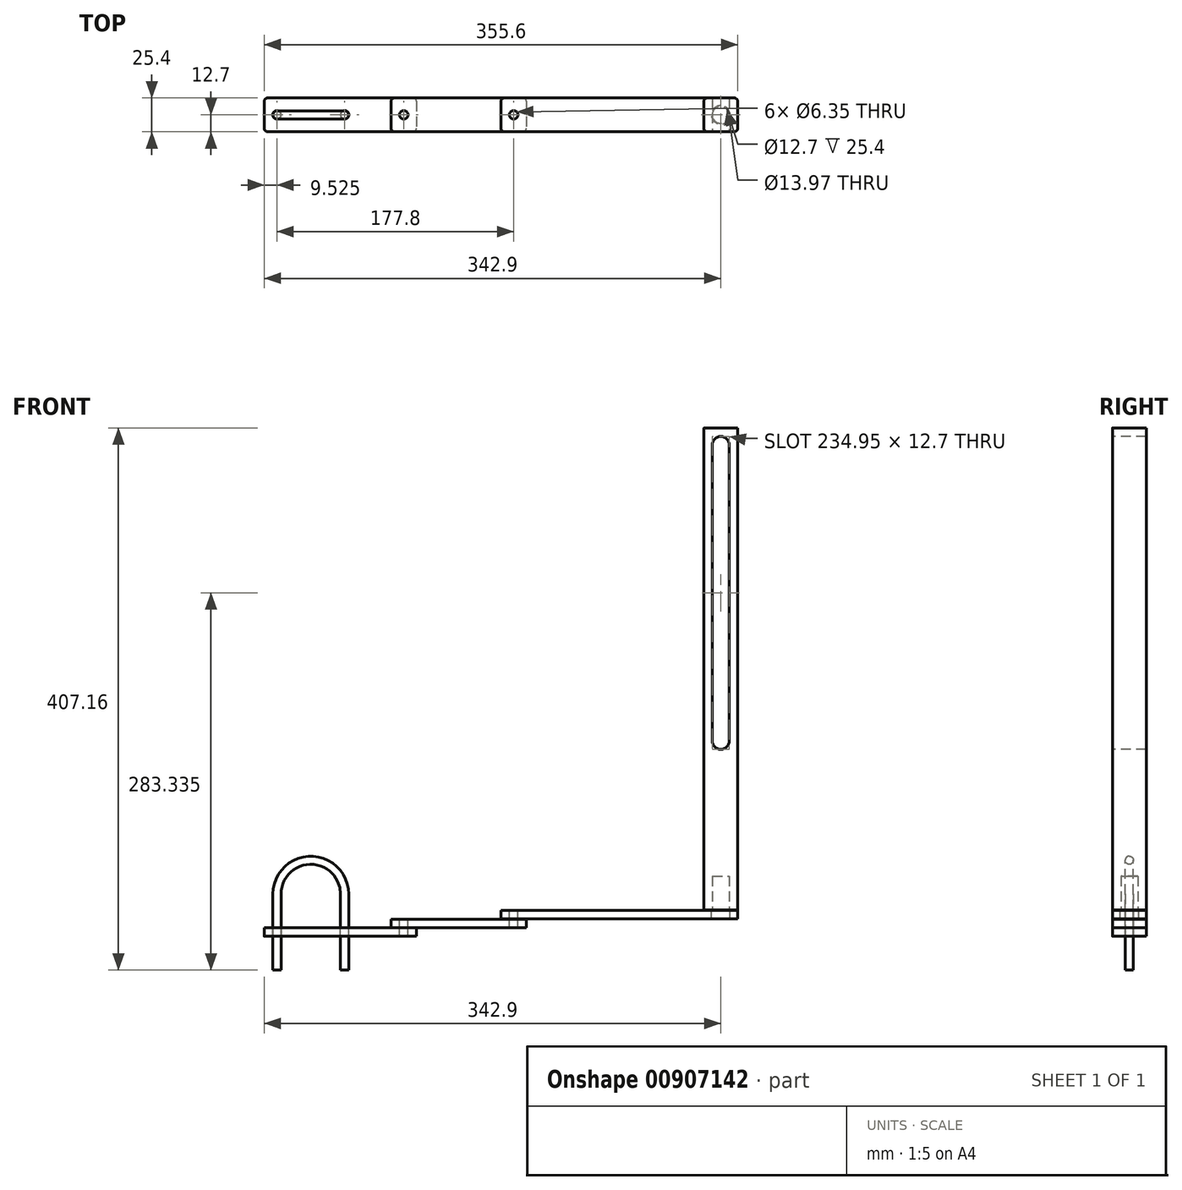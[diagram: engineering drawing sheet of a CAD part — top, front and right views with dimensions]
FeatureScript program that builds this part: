
annotation { "Feature Type Name" : "Feature", "Feature Type Description" : "" }
export const myFeature = defineFeature(function(context is Context, id is Id, definition is map)
    precondition{}
    {
        {
            var Q0;
            Q0=qCreatedBy(makeId("Front.planeOp"),FACE);
            var sketch = newSketch(context, id + "F0", { "sketchPlane" : qUnion([Q0])});
            skLineSegment(sketch, "E0.bottom", {"start": v(0, 0) * mm, "end": v(-25.4, 0) * mm});
            skLineSegment(sketch, "E0.top", {"start": v(0, 361.95) * mm, "end": v(-25.4, 361.95) * mm});
            skLineSegment(sketch, "E0.left", {"start": v(0, 0) * mm, "end": v(0, 361.95) * mm});
            skLineSegment(sketch, "E0.right", {"start": v(-25.4, 0) * mm, "end": v(-25.4, 361.95) * mm});
            skArc(sketch, "E1", {"start": v(-6.35, 349.25) * mm, "mid": v(-12.7, 355.6) * mm, "end": v(-19.05, 349.25) * mm});
            skArc(sketch, "E2", {"start": v(-19.05, 127) * mm, "mid": v(-12.7, 120.65) * mm, "end": v(-6.35, 127) * mm});
            skLineSegment(sketch, "E3", {"start": v(-19.05, 127) * mm, "end": v(-19.05, 349.25) * mm});
            skLineSegment(sketch, "E4", {"start": v(-6.35, 127) * mm, "end": v(-6.35, 349.25) * mm});
            skSolve(sketch);
        }
        {
            var Q0;
            Q0=makeQuery(id+"F0.imprint","IMPRINT",FACE,{"disambiguationData":[TD([[makeQuery(id+"F0.imprint","IMPRINT",EDGE,{"derivedFrom":sQuery(id+"F0.wireOp",EDGE,"E0.bottom")}),-1.0]])]});
            extrude(context, id + "F1", {"entities" : qUnion([Q0]), "oppositeDirection" : true, "depth" : 25.4 * mm, "offsetDistance" : 25.4 * mm});
        }
        {
            var Q0;
            Q0=makeQuery(id+"F1.opExtrude","SWEPT_FACE",FACE,{"disambiguationData":[OSD([sQuery(id+"F0.wireOp",EDGE,"E0.bottom")])]});
            var sketch = newSketch(context, id + "F2", { "sketchPlane" : qUnion([Q0])});
            skCircle(sketch, "E5", {"center": v(-12.7, -12.7) * mm, "radius": 6.35 * mm});
            skPoint(sketch, "E5.centerSnap0", {"position": v(-12.7, -25.4) * mm});
            skSolve(sketch);
        }
        {
            var Q0;
            Q0 = qSketchRegion(id + "F2", true);
            extrude(context, id + "F3", {"entities" : qUnion([Q0]), "operationType" : NewBodyOperationType.REMOVE, "oppositeDirection" : true, "depth" : 25.4 * mm, "offsetDistance" : 25.4 * mm});
        }
        {
            var Q0;
            Q0=makeQuery(id+"F1.opExtrude","SWEPT_FACE",FACE,{"disambiguationData":[OSD([sQuery(id+"F0.wireOp",EDGE,"E0.bottom")])]});
            cPlane(context, id + "F4", {"entities" : qUnion([Q0]), "cplaneType" : CPlaneType.OFFSET, "offset" : 0.25 * mm, "width" : 152.4 * mm, "height" : 152.4 * mm});
        }
        {
            var Q0;
            Q0=qCreatedBy(id+"F4.planeOp",FACE);
            var sketch = newSketch(context, id + "F5", { "sketchPlane" : qUnion([Q0])});
            skLineSegment(sketch, "E6.bottom", {"start": v(-2.54, 0) * mm, "end": v(-175.26, 0) * mm});
            skLineSegment(sketch, "E6.top", {"start": v(-2.54, -25.4) * mm, "end": v(-175.26, -25.4) * mm});
            skLineSegment(sketch, "E6.left", {"start": v(0, -2.54) * mm, "end": v(0, -22.86) * mm});
            skLineSegment(sketch, "E6.right", {"start": v(-177.8, -2.54) * mm, "end": v(-177.8, -22.86) * mm});
            skCircle(sketch, "E7", {"center": v(-168.28, -12.7) * mm, "radius": 3.17 * mm});
            skCircle(sketch, "E8", {"center": v(-12.7, -12.7) * mm, "radius": 6.99 * mm});
            skPoint(sketch, "E9.visualSharp", {"position": v(-177.8, 0) * mm});
            skArc(sketch, "E9.filletArc", {"start": v(-175.26, 0) * mm, "mid": v(-177.06, -0.74) * mm, "end": v(-177.8, -2.54) * mm});
            skPoint(sketch, "E10.visualSharp", {"position": v(-177.8, -25.4) * mm});
            skArc(sketch, "E10.filletArc", {"start": v(-177.8, -22.86) * mm, "mid": v(-177.06, -24.66) * mm, "end": v(-175.26, -25.4) * mm});
            skPoint(sketch, "E11.visualSharp", {"position": v(0, -25.4) * mm});
            skArc(sketch, "E11.filletArc", {"start": v(-2.54, -25.4) * mm, "mid": v(-0.74, -24.66) * mm, "end": v(0, -22.86) * mm});
            skPoint(sketch, "E12.visualSharp", {"position": v(0, 0) * mm});
            skArc(sketch, "E12.filletArc", {"start": v(0, -2.54) * mm, "mid": v(-0.74, -0.74) * mm, "end": v(-2.54, 0) * mm});
            skSolve(sketch);
        }
        {
            var Q0;
            Q0 = qSketchRegion(id + "F5", true);
            extrude(context, id + "F6", {"entities" : qUnion([Q0]), "depth" : 6.35 * mm, "offsetDistance" : 25.4 * mm});
        }
        {
            var Q0;
            Q0=makeQuery(id+"F1.opExtrude","CAP_EDGE",EDGE,{"disambiguationData":[OSD([sQuery(id+"F0.wireOp",EDGE,"E0.right")])],"isStart":true});
            var Q1;
            Q1=makeQuery(id+"F1.opExtrude","CAP_EDGE",EDGE,{"disambiguationData":[OSD([sQuery(id+"F0.wireOp",EDGE,"E0.right")])],"isStart":false});
            var Q2;
            Q2=makeQuery(id+"F1.opExtrude","CAP_EDGE",EDGE,{"disambiguationData":[OSD([sQuery(id+"F0.wireOp",EDGE,"E0.left")])],"isStart":true});
            var Q3;
            Q3=makeQuery(id+"F1.opExtrude","CAP_EDGE",EDGE,{"disambiguationData":[OSD([sQuery(id+"F0.wireOp",EDGE,"E0.left")])],"isStart":false});
            fillet(context, id + "F7", {"entities" : qUnion([Q0, Q1, Q2, Q3]), "radius" : 2.54 * mm, "tangentPropagation" : true, "allowEdgeOverflow" : false});
        }
        {
            var Q0;
            Q0=makeQuery(id+"F6.opExtrude","CAP_FACE",FACE,{"disambiguationData":[OSD([sQuery(id+"F5.wireOp",EDGE,"E6.bottom"),sQuery(id+"F5.wireOp",EDGE,"E6.top"),sQuery(id+"F5.wireOp",EDGE,"E6.left"),sQuery(id+"F5.wireOp",EDGE,"E6.right"),sQuery(id+"F5.wireOp",EDGE,"E7"),sQuery(id+"F5.wireOp",EDGE,"E8"),sQuery(id+"F5.wireOp",EDGE,"E9.filletArc"),sQuery(id+"F5.wireOp",EDGE,"E10.filletArc"),sQuery(id+"F5.wireOp",EDGE,"E11.filletArc"),sQuery(id+"F5.wireOp",EDGE,"E12.filletArc")])],"isStart":false});
            cPlane(context, id + "F8", {"entities" : qUnion([Q0]), "cplaneType" : CPlaneType.OFFSET, "offset" : 0.25 * mm, "width" : 152.4 * mm, "height" : 152.4 * mm});
        }
        {
            var Q0;
            Q0=qCreatedBy(id+"F8.planeOp",FACE);
            var sketch = newSketch(context, id + "F9", { "sketchPlane" : qUnion([Q0])});
            skLineSegment(sketch, "E13.bottom", {"start": v(-161.29, -25.4) * mm, "end": v(-257.81, -25.4) * mm});
            skLineSegment(sketch, "E13.top", {"start": v(-161.29, 0) * mm, "end": v(-257.81, 0) * mm});
            skLineSegment(sketch, "E13.left", {"start": v(-158.75, -22.86) * mm, "end": v(-158.75, -2.54) * mm});
            skLineSegment(sketch, "E13.right", {"start": v(-260.35, -22.86) * mm, "end": v(-260.35, -2.54) * mm});
            skCircle(sketch, "E14", {"center": v(-250.83, -12.7) * mm, "radius": 3.18 * mm});
            skCircle(sketch, "E15", {"center": v(-168.28, -12.7) * mm, "radius": 3.18 * mm});
            skPoint(sketch, "E16.visualSharp", {"position": v(-158.75, 0) * mm});
            skArc(sketch, "E16.filletArc", {"start": v(-158.75, -2.54) * mm, "mid": v(-159.5, -0.74) * mm, "end": v(-161.29, 0) * mm});
            skPoint(sketch, "E17.visualSharp", {"position": v(-158.75, -25.4) * mm});
            skArc(sketch, "E17.filletArc", {"start": v(-161.29, -25.4) * mm, "mid": v(-159.5, -24.66) * mm, "end": v(-158.75, -22.86) * mm});
            skPoint(sketch, "E18.visualSharp", {"position": v(-260.35, 0) * mm});
            skArc(sketch, "E18.filletArc", {"start": v(-257.81, 0) * mm, "mid": v(-259.6, -0.74) * mm, "end": v(-260.35, -2.54) * mm});
            skPoint(sketch, "E19.visualSharp", {"position": v(-260.35, -25.4) * mm});
            skArc(sketch, "E19.filletArc", {"start": v(-260.35, -22.86) * mm, "mid": v(-259.6, -24.66) * mm, "end": v(-257.81, -25.4) * mm});
            skSolve(sketch);
        }
        {
            var Q0;
            Q0 = qSketchRegion(id + "F9", true);
            extrude(context, id + "F10", {"entities" : qUnion([Q0]), "depth" : 6.35 * mm, "offsetDistance" : 25.4 * mm});
        }
        {
            var Q0;
            Q0=makeQuery(id+"F10.opExtrude","CAP_FACE",FACE,{"disambiguationData":[OSD([sQuery(id+"F9.wireOp",EDGE,"E13.bottom"),sQuery(id+"F9.wireOp",EDGE,"E13.top"),sQuery(id+"F9.wireOp",EDGE,"E13.left"),sQuery(id+"F9.wireOp",EDGE,"E13.right"),sQuery(id+"F9.wireOp",EDGE,"E14"),sQuery(id+"F9.wireOp",EDGE,"E15"),sQuery(id+"F9.wireOp",EDGE,"E16.filletArc"),sQuery(id+"F9.wireOp",EDGE,"E17.filletArc"),sQuery(id+"F9.wireOp",EDGE,"E18.filletArc"),sQuery(id+"F9.wireOp",EDGE,"E19.filletArc")])],"isStart":false});
            cPlane(context, id + "F11", {"entities" : qUnion([Q0]), "cplaneType" : CPlaneType.OFFSET, "offset" : 0.25 * mm, "width" : 152.4 * mm, "height" : 152.4 * mm});
        }
        {
            var Q0;
            Q0=qCreatedBy(id+"F11.planeOp",FACE);
            var sketch = newSketch(context, id + "F12", { "sketchPlane" : qUnion([Q0])});
            skLineSegment(sketch, "E20.bottom", {"start": v(-243.84, -25.4) * mm, "end": v(-353.06, -25.4) * mm});
            skLineSegment(sketch, "E20.top", {"start": v(-243.84, 0) * mm, "end": v(-353.06, 0) * mm});
            skLineSegment(sketch, "E20.left", {"start": v(-241.3, -22.86) * mm, "end": v(-241.3, -2.54) * mm});
            skLineSegment(sketch, "E20.right", {"start": v(-355.6, -22.86) * mm, "end": v(-355.6, -2.54) * mm});
            skCircle(sketch, "E21", {"center": v(-346.08, -12.7) * mm, "radius": 3.18 * mm});
            skCircle(sketch, "E22", {"center": v(-250.83, -12.7) * mm, "radius": 3.18 * mm});
            skCircle(sketch, "E23", {"center": v(-295.28, -12.7) * mm, "radius": 3.18 * mm});
            skPoint(sketch, "E24.visualSharp", {"position": v(-355.6, 0) * mm});
            skArc(sketch, "E24.filletArc", {"start": v(-353.06, 0) * mm, "mid": v(-354.86, -0.74) * mm, "end": v(-355.6, -2.54) * mm});
            skPoint(sketch, "E25.visualSharp", {"position": v(-355.6, -25.4) * mm});
            skArc(sketch, "E25.filletArc", {"start": v(-355.6, -22.86) * mm, "mid": v(-354.86, -24.66) * mm, "end": v(-353.06, -25.4) * mm});
            skPoint(sketch, "E26.visualSharp", {"position": v(-241.3, -25.4) * mm});
            skArc(sketch, "E26.filletArc", {"start": v(-243.84, -25.4) * mm, "mid": v(-242.04, -24.66) * mm, "end": v(-241.3, -22.86) * mm});
            skPoint(sketch, "E27.visualSharp", {"position": v(-241.3, 0) * mm});
            skArc(sketch, "E27.filletArc", {"start": v(-241.3, -2.54) * mm, "mid": v(-242.04, -0.74) * mm, "end": v(-243.84, 0) * mm});
            skSolve(sketch);
        }
        {
            var Q0;
            Q0 = qSketchRegion(id + "F12", true);
            extrude(context, id + "F13", {"entities" : qUnion([Q0]), "depth" : 6.35 * mm, "offsetDistance" : 25.4 * mm});
        }
        {
            var Q0;
            Q0=qCreatedBy(makeId("Front.planeOp"),FACE);
            cPlane(context, id + "F14", {"entities" : qUnion([Q0]), "cplaneType" : CPlaneType.OFFSET, "offset" : 12.7 * mm, "oppositeDirection" : true, "width" : 152.4 * mm, "height" : 152.4 * mm});
        }
        {
            var Q0;
            Q0=qCreatedBy(id+"F14.planeOp",FACE);
            var sketch = newSketch(context, id + "F15", { "sketchPlane" : qUnion([Q0])});
            skArc(sketch, "E28", {"start": v(-295.28, 11.94) * mm, "mid": v(-320.68, 37.34) * mm, "end": v(-346.08, 11.94) * mm});
            skLineSegment(sketch, "E29", {"start": v(-295.28, 11.94) * mm, "end": v(-295.28, -45.21) * mm});
            skLineSegment(sketch, "E30", {"start": v(-346.08, 11.94) * mm, "end": v(-346.08, -45.21) * mm});
            skSolve(sketch);
        }
        {
            var Q0;
            Q0=makeQuery(id+"F13.opExtrude","CAP_FACE",FACE,{"disambiguationData":[OSD([sQuery(id+"F12.wireOp",EDGE,"E20.bottom"),sQuery(id+"F12.wireOp",EDGE,"E20.top"),sQuery(id+"F12.wireOp",EDGE,"E20.left"),sQuery(id+"F12.wireOp",EDGE,"E20.right"),sQuery(id+"F12.wireOp",EDGE,"E21"),sQuery(id+"F12.wireOp",EDGE,"E22"),sQuery(id+"F12.wireOp",EDGE,"E23"),sQuery(id+"F12.wireOp",EDGE,"E24.filletArc"),sQuery(id+"F12.wireOp",EDGE,"E25.filletArc"),sQuery(id+"F12.wireOp",EDGE,"E26.filletArc"),sQuery(id+"F12.wireOp",EDGE,"E27.filletArc")])],"isStart":true});
            var sketch = newSketch(context, id + "F16", { "sketchPlane" : qUnion([Q0])});
            skCircle(sketch, "E31", {"center": v(-295.28, 12.7) * mm, "radius": 3.05 * mm});
            skSolve(sketch);
        }
        {
            var Q0;
            Q0=makeQuery(id+"F16.imprint","IMPRINT",FACE,{"disambiguationData":[TD([[makeQuery(id+"F16.imprint","IMPRINT",EDGE,{"derivedFrom":sQuery(id+"F16.wireOp",EDGE,"E31")}),1.0]])]});
            var Q1;
            Q1=sQuery(id+"F15.wireOp",EDGE,"E29");
            var Q2;
            Q2=sQuery(id+"F15.wireOp",EDGE,"E28");
            var Q3;
            Q3=sQuery(id+"F15.wireOp",EDGE,"E30");
            sweep(context, id + "F17", {"profiles" : qUnion([Q0]), "path" : qUnion([Q1, Q2, Q3])});
        }
    });
